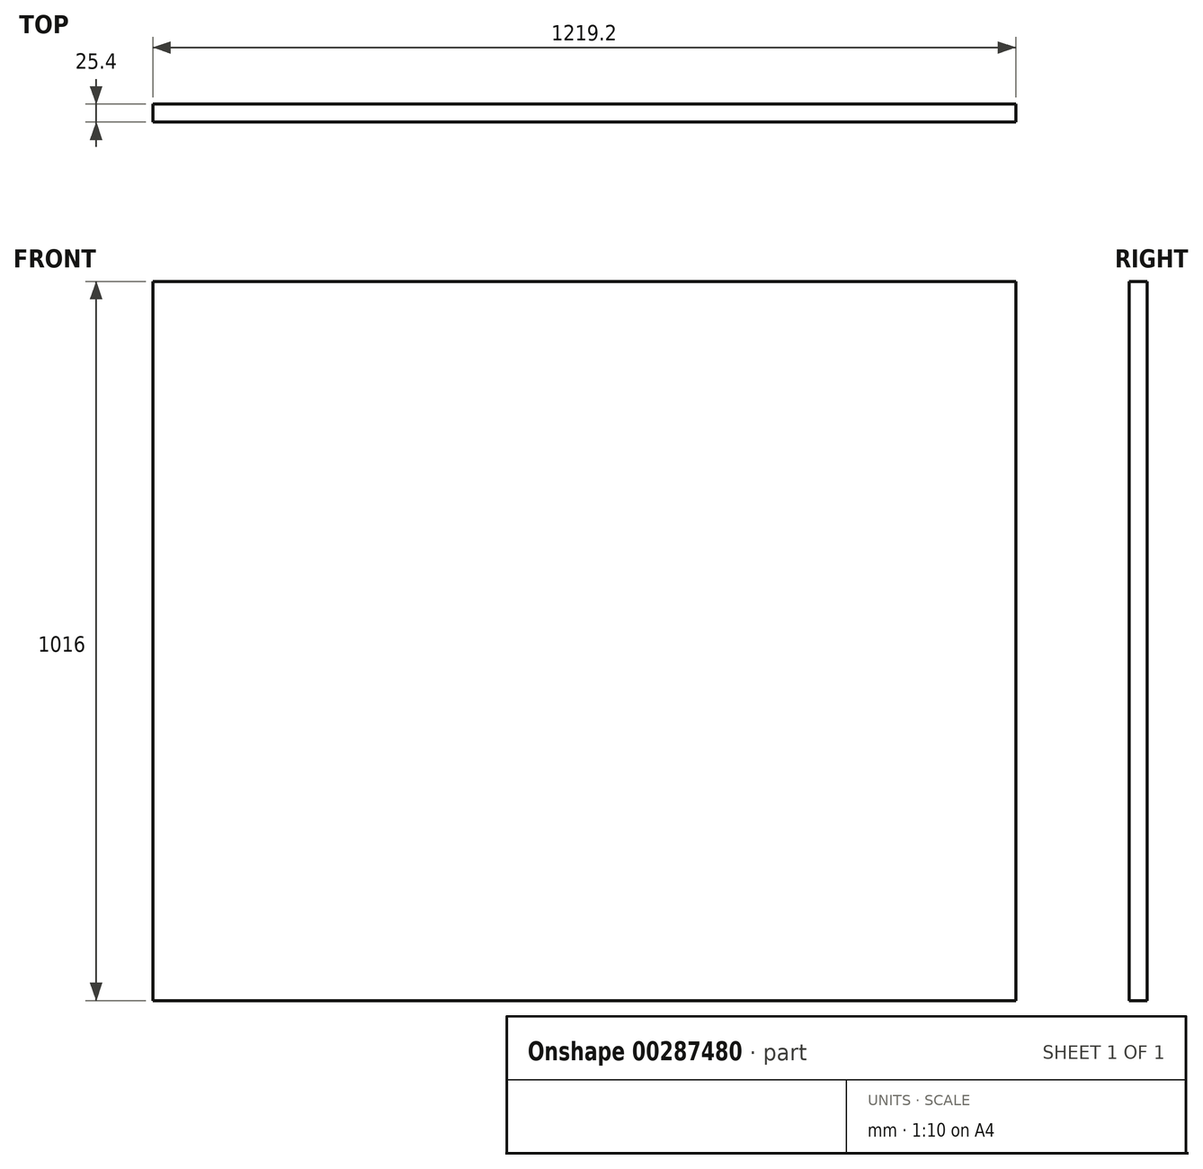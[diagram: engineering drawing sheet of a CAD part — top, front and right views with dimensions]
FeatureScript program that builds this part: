
annotation { "Feature Type Name" : "Feature", "Feature Type Description" : "" }
export const myFeature = defineFeature(function(context is Context, id is Id, definition is map)
    precondition{}
    {
        {
            var Q0;
            Q0=qCreatedBy(makeId("Front.planeOp"),FACE);
            var sketch = newSketch(context, id + "F0", { "sketchPlane" : qUnion([Q0])});
            skLineSegment(sketch, "E0.bottom", {"start": v(0, 0) * mm, "end": v(1219.2, 0) * mm});
            skLineSegment(sketch, "E0.top", {"start": v(0, -1016) * mm, "end": v(1219.2, -1016) * mm});
            skLineSegment(sketch, "E0.left", {"start": v(0, 0) * mm, "end": v(0, -1016) * mm});
            skLineSegment(sketch, "E0.right", {"start": v(1219.2, 0) * mm, "end": v(1219.2, -1016) * mm});
            skSolve(sketch);
        }
        {
            var Q0;
            Q0=qSketchRegion(id+"F0",true);
            extrude(context, id + "F1", {"entities" : qUnion([Q0]), "oppositeDirection" : true, "depth" : 25.4 * mm});
        }
    });
